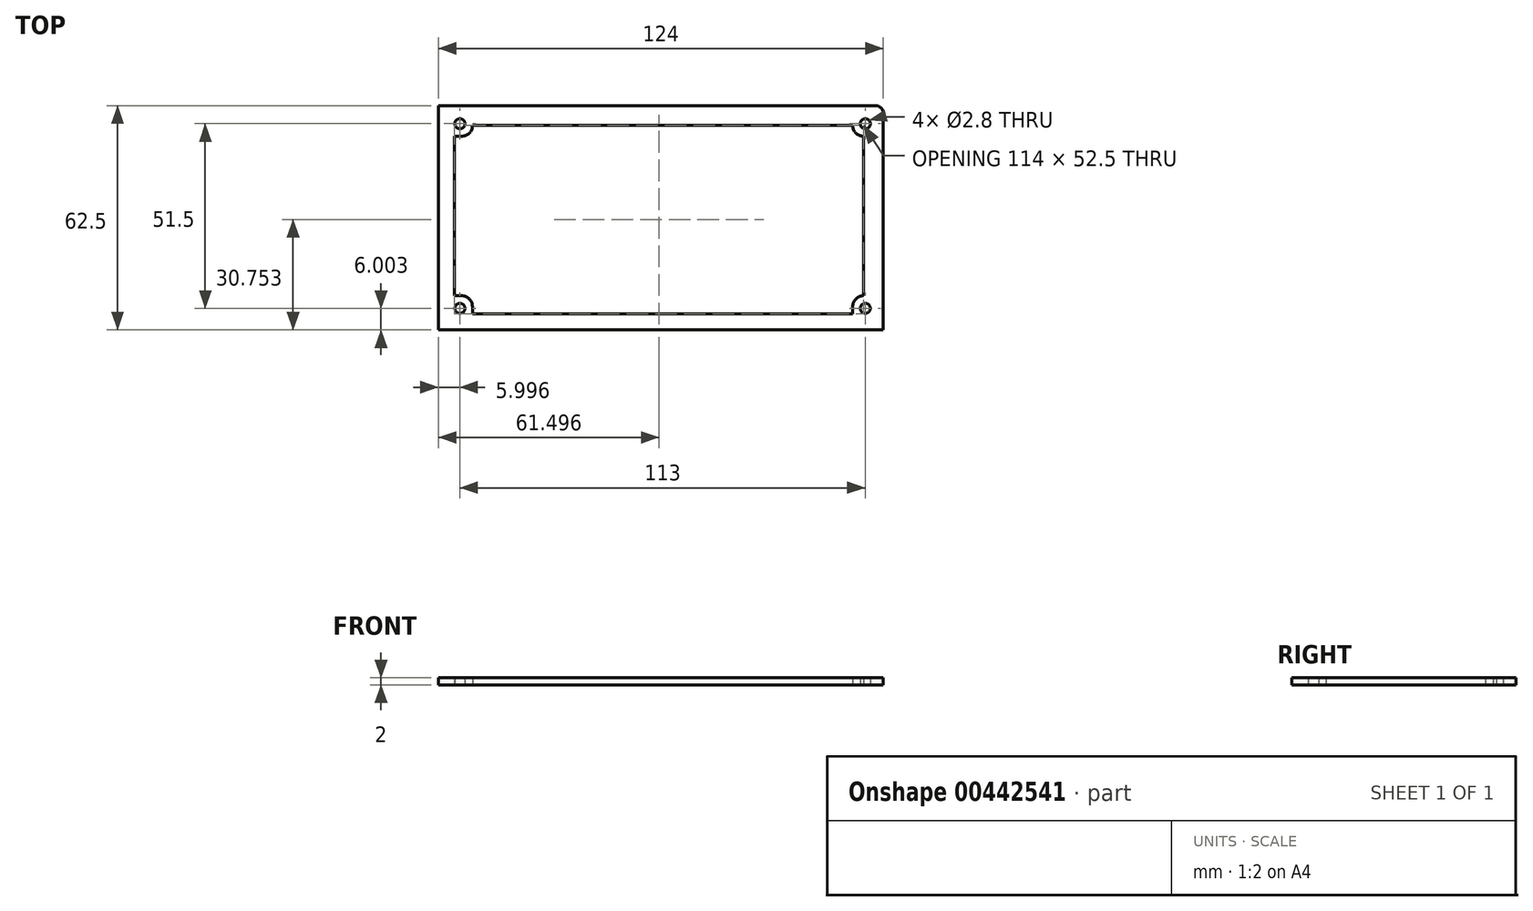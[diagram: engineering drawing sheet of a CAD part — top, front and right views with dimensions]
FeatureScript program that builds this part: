
annotation { "Feature Type Name" : "Feature", "Feature Type Description" : "" }
export const myFeature = defineFeature(function(context is Context, id is Id, definition is map)
    precondition{}
    {
        {
            var Q0;
            Q0=qCreatedBy(makeId("Top.planeOp"),FACE);
            var sketch = newSketch(context, id + "F0", { "sketchPlane" : qUnion([Q0])});
            skLineSegment(sketch, "E0.bottom", {"start": v(-72.45, 22.86) * mm, "end": v(71.55, 22.86) * mm});
            skLineSegment(sketch, "E0.top", {"start": v(-72.45, -61.14) * mm, "end": v(71.55, -61.14) * mm});
            skLineSegment(sketch, "E0.left", {"start": v(-74.45, 20.86) * mm, "end": v(-74.45, -59.14) * mm});
            skLineSegment(sketch, "E0.right", {"start": v(73.55, 20.86) * mm, "end": v(73.55, -59.14) * mm});
            skPoint(sketch, "E1.visualSharp", {"position": v(-74.45, 22.86) * mm});
            skArc(sketch, "E1.filletArc", {"start": v(-72.45, 22.86) * mm, "mid": v(-73.87, 22.28) * mm, "end": v(-74.45, 20.86) * mm});
            skPoint(sketch, "E2.visualSharp", {"position": v(73.55, 22.86) * mm});
            skArc(sketch, "E2.filletArc", {"start": v(73.55, 20.86) * mm, "mid": v(72.96, 22.28) * mm, "end": v(71.55, 22.86) * mm});
            skPoint(sketch, "E3.visualSharp", {"position": v(73.55, -61.14) * mm});
            skArc(sketch, "E3.filletArc", {"start": v(71.55, -61.14) * mm, "mid": v(72.96, -60.55) * mm, "end": v(73.55, -59.14) * mm});
            skPoint(sketch, "E4.visualSharp", {"position": v(-74.45, -61.14) * mm});
            skArc(sketch, "E4.filletArc", {"start": v(-74.45, -59.14) * mm, "mid": v(-73.87, -60.55) * mm, "end": v(-72.45, -61.14) * mm});
            skCircle(sketch, "E5", {"center": v(-69.45, 17.86) * mm, "radius": 1.4 * mm});
            skCircle(sketch, "E6", {"center": v(68.55, 17.86) * mm, "radius": 1.4 * mm});
            skCircle(sketch, "E7", {"center": v(-44.45, 17.86) * mm, "radius": 1.4 * mm});
            skCircle(sketch, "E8", {"center": v(-44.45, -33.64) * mm, "radius": 1.4 * mm});
            skCircle(sketch, "E9", {"center": v(68.55, -33.64) * mm, "radius": 1.4 * mm});
            skCircle(sketch, "E10", {"center": v(-69.45, -56.14) * mm, "radius": 1.4 * mm});
            skCircle(sketch, "E11", {"center": v(44.55, -56.14) * mm, "radius": 1.4 * mm});
            skLineSegment(sketch, "E12.top", {"start": v(-45.95, 14.36) * mm, "end": v(-43.95, 14.36) * mm});
            skLineSegment(sketch, "E13.top", {"start": v(-45.95, -30.14) * mm, "end": v(-43.95, -30.14) * mm});
            skLineSegment(sketch, "E13.right", {"start": v(-40.95, -35.14) * mm, "end": v(-40.95, -33.14) * mm});
            skLineSegment(sketch, "E14.right", {"start": v(65.05, -35.14) * mm, "end": v(65.05, -33.14) * mm});
            skLineSegment(sketch, "E15", {"start": v(65.05, -35.14) * mm, "end": v(-40.95, -35.14) * mm});
            skLineSegment(sketch, "E16", {"start": v(-45.95, -30.14) * mm, "end": v(-45.95, 14.36) * mm});
            skPoint(sketch, "E17.visualSharp", {"position": v(-40.95, 14.36) * mm});
            skArc(sketch, "E17.filletArc", {"start": v(-43.95, 14.36) * mm, "mid": v(-41.83, 15.24) * mm, "end": v(-40.95, 17.36) * mm});
            skPoint(sketch, "E18.visualSharp", {"position": v(65.05, 14.36) * mm});
            skArc(sketch, "E18.filletArc", {"start": v(65.05, 17.36) * mm, "mid": v(65.92, 15.24) * mm, "end": v(68.05, 14.36) * mm});
            skPoint(sketch, "E19.visualSharp", {"position": v(65.05, -30.14) * mm});
            skArc(sketch, "E19.filletArc", {"start": v(68.05, -30.14) * mm, "mid": v(65.92, -31.02) * mm, "end": v(65.05, -33.14) * mm});
            skPoint(sketch, "E20.visualSharp", {"position": v(-40.95, -30.14) * mm});
            skArc(sketch, "E20.filletArc", {"start": v(-40.95, -33.14) * mm, "mid": v(-41.83, -31.02) * mm, "end": v(-43.95, -30.14) * mm});
            skLineSegment(sketch, "E21", {"start": v(68.05, 14.36) * mm, "end": v(68.05, -30.14) * mm});
            skLineSegment(sketch, "E22", {"start": v(65.05, 17.36) * mm, "end": v(-40.95, 17.36) * mm});
            skLineSegment(sketch, "E23.bottom", {"start": v(-66.45, -39.64) * mm, "end": v(-61.95, -39.64) * mm});
            skLineSegment(sketch, "E23.top", {"start": v(-66.45, -44.14) * mm, "end": v(-61.95, -44.14) * mm});
            skLineSegment(sketch, "E23.left", {"start": v(-66.45, -39.64) * mm, "end": v(-66.45, -44.14) * mm});
            skLineSegment(sketch, "E23.right", {"start": v(-61.95, -39.64) * mm, "end": v(-61.95, -44.14) * mm});
            skLineSegment(sketch, "E24.bottom", {"start": v(-66.39, -47.2) * mm, "end": v(-61.89, -47.2) * mm});
            skLineSegment(sketch, "E24.top", {"start": v(-66.39, -51.7) * mm, "end": v(-61.89, -51.7) * mm});
            skLineSegment(sketch, "E24.left", {"start": v(-66.39, -47.2) * mm, "end": v(-66.39, -51.7) * mm});
            skLineSegment(sketch, "E24.right", {"start": v(-61.89, -47.2) * mm, "end": v(-61.89, -51.7) * mm});
            skLineSegment(sketch, "E25.1.0.0", {"start": v(-53.89, -47.2) * mm, "end": v(-53.89, -51.7) * mm});
            skLineSegment(sketch, "E25.1.0.1", {"start": v(-58.39, -47.2) * mm, "end": v(-58.39, -51.7) * mm});
            skLineSegment(sketch, "E25.1.0.2", {"start": v(-58.39, -51.7) * mm, "end": v(-53.89, -51.7) * mm});
            skLineSegment(sketch, "E25.1.0.3", {"start": v(-58.39, -47.2) * mm, "end": v(-53.89, -47.2) * mm});
            skLineSegment(sketch, "E25.1.0.4", {"start": v(-53.95, -39.64) * mm, "end": v(-53.95, -44.14) * mm});
            skLineSegment(sketch, "E25.1.0.5", {"start": v(-58.45, -44.14) * mm, "end": v(-53.95, -44.14) * mm});
            skLineSegment(sketch, "E25.1.0.6", {"start": v(-58.45, -39.64) * mm, "end": v(-58.45, -44.14) * mm});
            skLineSegment(sketch, "E25.1.0.7", {"start": v(-58.45, -39.64) * mm, "end": v(-53.95, -39.64) * mm});
            skLineSegment(sketch, "E25.2.0.0", {"start": v(-45.89, -47.2) * mm, "end": v(-45.89, -51.7) * mm});
            skLineSegment(sketch, "E25.2.0.1", {"start": v(-50.39, -47.2) * mm, "end": v(-50.39, -51.7) * mm});
            skLineSegment(sketch, "E25.2.0.2", {"start": v(-50.39, -51.7) * mm, "end": v(-45.89, -51.7) * mm});
            skLineSegment(sketch, "E25.2.0.3", {"start": v(-50.39, -47.2) * mm, "end": v(-45.89, -47.2) * mm});
            skLineSegment(sketch, "E25.2.0.4", {"start": v(-45.95, -39.64) * mm, "end": v(-45.95, -44.14) * mm});
            skLineSegment(sketch, "E25.2.0.5", {"start": v(-50.45, -44.14) * mm, "end": v(-45.95, -44.14) * mm});
            skLineSegment(sketch, "E25.2.0.6", {"start": v(-50.45, -39.64) * mm, "end": v(-50.45, -44.14) * mm});
            skLineSegment(sketch, "E25.2.0.7", {"start": v(-50.45, -39.64) * mm, "end": v(-45.95, -39.64) * mm});
            skLineSegment(sketch, "E25.3.0.0", {"start": v(-37.89, -47.2) * mm, "end": v(-37.89, -51.7) * mm});
            skLineSegment(sketch, "E25.3.0.1", {"start": v(-42.39, -47.2) * mm, "end": v(-42.39, -51.7) * mm});
            skLineSegment(sketch, "E25.3.0.2", {"start": v(-42.39, -51.7) * mm, "end": v(-37.89, -51.7) * mm});
            skLineSegment(sketch, "E25.3.0.3", {"start": v(-42.39, -47.2) * mm, "end": v(-37.89, -47.2) * mm});
            skLineSegment(sketch, "E25.3.0.4", {"start": v(-37.95, -39.64) * mm, "end": v(-37.95, -44.14) * mm});
            skLineSegment(sketch, "E25.3.0.5", {"start": v(-42.45, -44.14) * mm, "end": v(-37.95, -44.14) * mm});
            skLineSegment(sketch, "E25.3.0.6", {"start": v(-42.45, -39.64) * mm, "end": v(-42.45, -44.14) * mm});
            skLineSegment(sketch, "E25.3.0.7", {"start": v(-42.45, -39.64) * mm, "end": v(-37.95, -39.64) * mm});
            skLineSegment(sketch, "E25.4.0.0", {"start": v(-29.89, -47.2) * mm, "end": v(-29.89, -51.7) * mm});
            skLineSegment(sketch, "E25.4.0.1", {"start": v(-34.39, -47.2) * mm, "end": v(-34.39, -51.7) * mm});
            skLineSegment(sketch, "E25.4.0.2", {"start": v(-34.39, -51.7) * mm, "end": v(-29.89, -51.7) * mm});
            skLineSegment(sketch, "E25.4.0.3", {"start": v(-34.39, -47.2) * mm, "end": v(-29.89, -47.2) * mm});
            skLineSegment(sketch, "E25.4.0.4", {"start": v(-29.95, -39.64) * mm, "end": v(-29.95, -44.14) * mm});
            skLineSegment(sketch, "E25.4.0.5", {"start": v(-34.45, -44.14) * mm, "end": v(-29.95, -44.14) * mm});
            skLineSegment(sketch, "E25.4.0.6", {"start": v(-34.45, -39.64) * mm, "end": v(-34.45, -44.14) * mm});
            skLineSegment(sketch, "E25.4.0.7", {"start": v(-34.45, -39.64) * mm, "end": v(-29.95, -39.64) * mm});
            skLineSegment(sketch, "E25.5.0.0", {"start": v(-21.89, -47.2) * mm, "end": v(-21.89, -51.7) * mm});
            skLineSegment(sketch, "E25.5.0.1", {"start": v(-26.39, -47.2) * mm, "end": v(-26.39, -51.7) * mm});
            skLineSegment(sketch, "E25.5.0.2", {"start": v(-26.39, -51.7) * mm, "end": v(-21.89, -51.7) * mm});
            skLineSegment(sketch, "E25.5.0.3", {"start": v(-26.39, -47.2) * mm, "end": v(-21.89, -47.2) * mm});
            skLineSegment(sketch, "E25.5.0.4", {"start": v(-21.95, -39.64) * mm, "end": v(-21.95, -44.14) * mm});
            skLineSegment(sketch, "E25.5.0.5", {"start": v(-26.45, -44.14) * mm, "end": v(-21.95, -44.14) * mm});
            skLineSegment(sketch, "E25.5.0.6", {"start": v(-26.45, -39.64) * mm, "end": v(-26.45, -44.14) * mm});
            skLineSegment(sketch, "E25.5.0.7", {"start": v(-26.45, -39.64) * mm, "end": v(-21.95, -39.64) * mm});
            skLineSegment(sketch, "E25.6.0.0", {"start": v(-13.89, -47.2) * mm, "end": v(-13.89, -51.7) * mm});
            skLineSegment(sketch, "E25.6.0.1", {"start": v(-18.39, -47.2) * mm, "end": v(-18.39, -51.7) * mm});
            skLineSegment(sketch, "E25.6.0.2", {"start": v(-18.39, -51.7) * mm, "end": v(-13.89, -51.7) * mm});
            skLineSegment(sketch, "E25.6.0.3", {"start": v(-18.39, -47.2) * mm, "end": v(-13.89, -47.2) * mm});
            skLineSegment(sketch, "E25.6.0.4", {"start": v(-13.95, -39.64) * mm, "end": v(-13.95, -44.14) * mm});
            skLineSegment(sketch, "E25.6.0.5", {"start": v(-18.45, -44.14) * mm, "end": v(-13.95, -44.14) * mm});
            skLineSegment(sketch, "E25.6.0.6", {"start": v(-18.45, -39.64) * mm, "end": v(-18.45, -44.14) * mm});
            skLineSegment(sketch, "E25.6.0.7", {"start": v(-18.45, -39.64) * mm, "end": v(-13.95, -39.64) * mm});
            skLineSegment(sketch, "E25.7.0.0", {"start": v(-5.89, -47.2) * mm, "end": v(-5.89, -51.7) * mm});
            skLineSegment(sketch, "E25.7.0.1", {"start": v(-10.39, -47.2) * mm, "end": v(-10.39, -51.7) * mm});
            skLineSegment(sketch, "E25.7.0.2", {"start": v(-10.39, -51.7) * mm, "end": v(-5.89, -51.7) * mm});
            skLineSegment(sketch, "E25.7.0.3", {"start": v(-10.39, -47.2) * mm, "end": v(-5.89, -47.2) * mm});
            skLineSegment(sketch, "E25.7.0.4", {"start": v(-5.95, -39.64) * mm, "end": v(-5.95, -44.14) * mm});
            skLineSegment(sketch, "E25.7.0.5", {"start": v(-10.45, -44.14) * mm, "end": v(-5.95, -44.14) * mm});
            skLineSegment(sketch, "E25.7.0.6", {"start": v(-10.45, -39.64) * mm, "end": v(-10.45, -44.14) * mm});
            skLineSegment(sketch, "E25.7.0.7", {"start": v(-10.45, -39.64) * mm, "end": v(-5.95, -39.64) * mm});
            skLineSegment(sketch, "E25.8.0.0", {"start": v(2.11, -47.2) * mm, "end": v(2.11, -51.7) * mm});
            skLineSegment(sketch, "E25.8.0.1", {"start": v(-2.39, -47.2) * mm, "end": v(-2.39, -51.7) * mm});
            skLineSegment(sketch, "E25.8.0.2", {"start": v(-2.39, -51.7) * mm, "end": v(2.11, -51.7) * mm});
            skLineSegment(sketch, "E25.8.0.3", {"start": v(-2.39, -47.2) * mm, "end": v(2.11, -47.2) * mm});
            skLineSegment(sketch, "E25.8.0.4", {"start": v(2.05, -39.64) * mm, "end": v(2.05, -44.14) * mm});
            skLineSegment(sketch, "E25.8.0.5", {"start": v(-2.45, -44.14) * mm, "end": v(2.05, -44.14) * mm});
            skLineSegment(sketch, "E25.8.0.6", {"start": v(-2.45, -39.64) * mm, "end": v(-2.45, -44.14) * mm});
            skLineSegment(sketch, "E25.8.0.7", {"start": v(-2.45, -39.64) * mm, "end": v(2.05, -39.64) * mm});
            skLineSegment(sketch, "E25.9.0.0", {"start": v(10.11, -47.2) * mm, "end": v(10.11, -51.7) * mm});
            skLineSegment(sketch, "E25.9.0.1", {"start": v(5.61, -47.2) * mm, "end": v(5.61, -51.7) * mm});
            skLineSegment(sketch, "E25.9.0.2", {"start": v(5.61, -51.7) * mm, "end": v(10.11, -51.7) * mm});
            skLineSegment(sketch, "E25.9.0.3", {"start": v(5.61, -47.2) * mm, "end": v(10.11, -47.2) * mm});
            skLineSegment(sketch, "E25.9.0.4", {"start": v(10.05, -39.64) * mm, "end": v(10.05, -44.14) * mm});
            skLineSegment(sketch, "E25.9.0.5", {"start": v(5.55, -44.14) * mm, "end": v(10.05, -44.14) * mm});
            skLineSegment(sketch, "E25.9.0.6", {"start": v(5.55, -39.64) * mm, "end": v(5.55, -44.14) * mm});
            skLineSegment(sketch, "E25.9.0.7", {"start": v(5.55, -39.64) * mm, "end": v(10.05, -39.64) * mm});
            skLineSegment(sketch, "E25.10.0.0", {"start": v(18.11, -47.2) * mm, "end": v(18.11, -51.7) * mm});
            skLineSegment(sketch, "E25.10.0.1", {"start": v(13.61, -47.2) * mm, "end": v(13.61, -51.7) * mm});
            skLineSegment(sketch, "E25.10.0.2", {"start": v(13.61, -51.7) * mm, "end": v(18.11, -51.7) * mm});
            skLineSegment(sketch, "E25.10.0.3", {"start": v(13.61, -47.2) * mm, "end": v(18.11, -47.2) * mm});
            skLineSegment(sketch, "E25.10.0.4", {"start": v(18.05, -39.64) * mm, "end": v(18.05, -44.14) * mm});
            skLineSegment(sketch, "E25.10.0.5", {"start": v(13.55, -44.14) * mm, "end": v(18.05, -44.14) * mm});
            skLineSegment(sketch, "E25.10.0.6", {"start": v(13.55, -39.64) * mm, "end": v(13.55, -44.14) * mm});
            skLineSegment(sketch, "E25.10.0.7", {"start": v(13.55, -39.64) * mm, "end": v(18.05, -39.64) * mm});
            skLineSegment(sketch, "E25.11.0.0", {"start": v(26.11, -47.2) * mm, "end": v(26.11, -51.7) * mm});
            skLineSegment(sketch, "E25.11.0.1", {"start": v(21.61, -47.2) * mm, "end": v(21.61, -51.7) * mm});
            skLineSegment(sketch, "E25.11.0.2", {"start": v(21.61, -51.7) * mm, "end": v(26.11, -51.7) * mm});
            skLineSegment(sketch, "E25.11.0.3", {"start": v(21.61, -47.2) * mm, "end": v(26.11, -47.2) * mm});
            skLineSegment(sketch, "E25.11.0.4", {"start": v(26.05, -39.64) * mm, "end": v(26.05, -44.14) * mm});
            skLineSegment(sketch, "E25.11.0.5", {"start": v(21.55, -44.14) * mm, "end": v(26.05, -44.14) * mm});
            skLineSegment(sketch, "E25.11.0.6", {"start": v(21.55, -39.64) * mm, "end": v(21.55, -44.14) * mm});
            skLineSegment(sketch, "E25.11.0.7", {"start": v(21.55, -39.64) * mm, "end": v(26.05, -39.64) * mm});
            skLineSegment(sketch, "E25.12.0.0", {"start": v(34.11, -47.2) * mm, "end": v(34.11, -51.7) * mm});
            skLineSegment(sketch, "E25.12.0.1", {"start": v(29.61, -47.2) * mm, "end": v(29.61, -51.7) * mm});
            skLineSegment(sketch, "E25.12.0.2", {"start": v(29.61, -51.7) * mm, "end": v(34.11, -51.7) * mm});
            skLineSegment(sketch, "E25.12.0.3", {"start": v(29.61, -47.2) * mm, "end": v(34.11, -47.2) * mm});
            skLineSegment(sketch, "E25.12.0.4", {"start": v(34.05, -39.64) * mm, "end": v(34.05, -44.14) * mm});
            skLineSegment(sketch, "E25.12.0.5", {"start": v(29.55, -44.14) * mm, "end": v(34.05, -44.14) * mm});
            skLineSegment(sketch, "E25.12.0.6", {"start": v(29.55, -39.64) * mm, "end": v(29.55, -44.14) * mm});
            skLineSegment(sketch, "E25.12.0.7", {"start": v(29.55, -39.64) * mm, "end": v(34.05, -39.64) * mm});
            skLineSegment(sketch, "E25.13.0.0", {"start": v(42.11, -47.2) * mm, "end": v(42.11, -51.7) * mm});
            skLineSegment(sketch, "E25.13.0.1", {"start": v(37.61, -47.2) * mm, "end": v(37.61, -51.7) * mm});
            skLineSegment(sketch, "E25.13.0.2", {"start": v(37.61, -51.7) * mm, "end": v(42.11, -51.7) * mm});
            skLineSegment(sketch, "E25.13.0.3", {"start": v(37.61, -47.2) * mm, "end": v(42.11, -47.2) * mm});
            skLineSegment(sketch, "E25.13.0.4", {"start": v(42.05, -39.64) * mm, "end": v(42.05, -44.14) * mm});
            skLineSegment(sketch, "E25.13.0.5", {"start": v(37.55, -44.14) * mm, "end": v(42.05, -44.14) * mm});
            skLineSegment(sketch, "E25.13.0.6", {"start": v(37.55, -39.64) * mm, "end": v(37.55, -44.14) * mm});
            skLineSegment(sketch, "E25.13.0.7", {"start": v(37.55, -39.64) * mm, "end": v(42.05, -39.64) * mm});
            skLineSegment(sketch, "E25.14.0.0", {"start": v(50.11, -47.2) * mm, "end": v(50.11, -51.7) * mm});
            skLineSegment(sketch, "E25.14.0.1", {"start": v(45.61, -47.2) * mm, "end": v(45.61, -51.7) * mm});
            skLineSegment(sketch, "E25.14.0.2", {"start": v(45.61, -51.7) * mm, "end": v(50.11, -51.7) * mm});
            skLineSegment(sketch, "E25.14.0.3", {"start": v(45.61, -47.2) * mm, "end": v(50.11, -47.2) * mm});
            skLineSegment(sketch, "E25.14.0.4", {"start": v(50.05, -39.64) * mm, "end": v(50.05, -44.14) * mm});
            skLineSegment(sketch, "E25.14.0.5", {"start": v(45.55, -44.14) * mm, "end": v(50.05, -44.14) * mm});
            skLineSegment(sketch, "E25.14.0.6", {"start": v(45.55, -39.64) * mm, "end": v(45.55, -44.14) * mm});
            skLineSegment(sketch, "E25.14.0.7", {"start": v(45.55, -39.64) * mm, "end": v(50.05, -39.64) * mm});
            skLineSegment(sketch, "E25.15.0.0", {"start": v(58.11, -47.2) * mm, "end": v(58.11, -51.7) * mm});
            skLineSegment(sketch, "E25.15.0.1", {"start": v(53.61, -47.2) * mm, "end": v(53.61, -51.7) * mm});
            skLineSegment(sketch, "E25.15.0.2", {"start": v(53.61, -51.7) * mm, "end": v(58.11, -51.7) * mm});
            skLineSegment(sketch, "E25.15.0.3", {"start": v(53.61, -47.2) * mm, "end": v(58.11, -47.2) * mm});
            skLineSegment(sketch, "E25.15.0.4", {"start": v(58.05, -39.64) * mm, "end": v(58.05, -44.14) * mm});
            skLineSegment(sketch, "E25.15.0.5", {"start": v(53.55, -44.14) * mm, "end": v(58.05, -44.14) * mm});
            skLineSegment(sketch, "E25.15.0.6", {"start": v(53.55, -39.64) * mm, "end": v(53.55, -44.14) * mm});
            skLineSegment(sketch, "E25.15.0.7", {"start": v(53.55, -39.64) * mm, "end": v(58.05, -39.64) * mm});
            skLineSegment(sketch, "E25.16.0.0", {"start": v(66.11, -47.2) * mm, "end": v(66.11, -51.7) * mm});
            skLineSegment(sketch, "E25.16.0.1", {"start": v(61.61, -47.2) * mm, "end": v(61.61, -51.7) * mm});
            skLineSegment(sketch, "E25.16.0.2", {"start": v(61.61, -51.7) * mm, "end": v(66.11, -51.7) * mm});
            skLineSegment(sketch, "E25.16.0.3", {"start": v(61.61, -47.2) * mm, "end": v(66.11, -47.2) * mm});
            skLineSegment(sketch, "E25.16.0.4", {"start": v(66.05, -39.64) * mm, "end": v(66.05, -44.14) * mm});
            skLineSegment(sketch, "E25.16.0.5", {"start": v(61.55, -44.14) * mm, "end": v(66.05, -44.14) * mm});
            skLineSegment(sketch, "E25.16.0.6", {"start": v(61.55, -39.64) * mm, "end": v(61.55, -44.14) * mm});
            skLineSegment(sketch, "E25.16.0.7", {"start": v(61.55, -39.64) * mm, "end": v(66.05, -39.64) * mm});
            skLineSegment(sketch, "E25.direction1", {"start": v(-66.39, -51.7) * mm, "end": v(-58.39, -51.7) * mm, "construction": true});
            skSolve(sketch);
        }
        {
            var Q0;
            Q0=makeQuery(id+"F0.imprint","IMPRINT",FACE,{"disambiguationData":[TD([[makeQuery(id+"F0.imprint","IMPRINT",EDGE,{"derivedFrom":sQuery(id+"F0.wireOp",EDGE,"E0.bottom")}),-1.0]])]});
            extrude(context, id + "F1", {"entities" : qUnion([Q0]), "depth" : 2 * mm});
        }
        {
            var Q0;
            Q0=makeQuery(id+"F1.opExtrude","CAP_FACE",FACE,{"disambiguationData":[OSD([sQuery(id+"F0.wireOp",EDGE,"E0.bottom"),sQuery(id+"F0.wireOp",EDGE,"E0.top"),sQuery(id+"F0.wireOp",EDGE,"E0.left"),sQuery(id+"F0.wireOp",EDGE,"E0.right"),sQuery(id+"F0.wireOp",EDGE,"E1.filletArc"),sQuery(id+"F0.wireOp",EDGE,"E2.filletArc"),sQuery(id+"F0.wireOp",EDGE,"E3.filletArc"),sQuery(id+"F0.wireOp",EDGE,"E4.filletArc"),sQuery(id+"F0.wireOp",EDGE,"E5"),sQuery(id+"F0.wireOp",EDGE,"E6"),sQuery(id+"F0.wireOp",EDGE,"E7"),sQuery(id+"F0.wireOp",EDGE,"E8"),sQuery(id+"F0.wireOp",EDGE,"E9"),sQuery(id+"F0.wireOp",EDGE,"E10"),sQuery(id+"F0.wireOp",EDGE,"E11"),sQuery(id+"F0.wireOp",EDGE,"E12.top"),sQuery(id+"F0.wireOp",EDGE,"E13.top"),sQuery(id+"F0.wireOp",EDGE,"E13.right"),sQuery(id+"F0.wireOp",EDGE,"E14.right"),sQuery(id+"F0.wireOp",EDGE,"E15"),sQuery(id+"F0.wireOp",EDGE,"E16"),sQuery(id+"F0.wireOp",EDGE,"E17.filletArc"),sQuery(id+"F0.wireOp",EDGE,"E18.filletArc"),sQuery(id+"F0.wireOp",EDGE,"E19.filletArc"),sQuery(id+"F0.wireOp",EDGE,"E20.filletArc"),sQuery(id+"F0.wireOp",EDGE,"E21"),sQuery(id+"F0.wireOp",EDGE,"E22"),sQuery(id+"F0.wireOp",EDGE,"E23.bottom"),sQuery(id+"F0.wireOp",EDGE,"E23.top"),sQuery(id+"F0.wireOp",EDGE,"E23.left"),sQuery(id+"F0.wireOp",EDGE,"E23.right"),sQuery(id+"F0.wireOp",EDGE,"E24.bottom"),sQuery(id+"F0.wireOp",EDGE,"E24.top"),sQuery(id+"F0.wireOp",EDGE,"E24.left"),sQuery(id+"F0.wireOp",EDGE,"E24.right"),sQuery(id+"F0.wireOp",EDGE,"E25.1.0.0"),sQuery(id+"F0.wireOp",EDGE,"E25.1.0.1"),sQuery(id+"F0.wireOp",EDGE,"E25.1.0.2"),sQuery(id+"F0.wireOp",EDGE,"E25.1.0.3"),sQuery(id+"F0.wireOp",EDGE,"E25.1.0.4"),sQuery(id+"F0.wireOp",EDGE,"E25.1.0.5"),sQuery(id+"F0.wireOp",EDGE,"E25.1.0.6"),sQuery(id+"F0.wireOp",EDGE,"E25.1.0.7"),sQuery(id+"F0.wireOp",EDGE,"E25.2.0.0"),sQuery(id+"F0.wireOp",EDGE,"E25.2.0.1"),sQuery(id+"F0.wireOp",EDGE,"E25.2.0.2"),sQuery(id+"F0.wireOp",EDGE,"E25.2.0.3"),sQuery(id+"F0.wireOp",EDGE,"E25.2.0.4"),sQuery(id+"F0.wireOp",EDGE,"E25.2.0.5"),sQuery(id+"F0.wireOp",EDGE,"E25.2.0.6"),sQuery(id+"F0.wireOp",EDGE,"E25.2.0.7"),sQuery(id+"F0.wireOp",EDGE,"E25.3.0.0"),sQuery(id+"F0.wireOp",EDGE,"E25.3.0.1"),sQuery(id+"F0.wireOp",EDGE,"E25.3.0.2"),sQuery(id+"F0.wireOp",EDGE,"E25.3.0.3"),sQuery(id+"F0.wireOp",EDGE,"E25.3.0.4"),sQuery(id+"F0.wireOp",EDGE,"E25.3.0.5"),sQuery(id+"F0.wireOp",EDGE,"E25.3.0.6"),sQuery(id+"F0.wireOp",EDGE,"E25.3.0.7"),sQuery(id+"F0.wireOp",EDGE,"E25.4.0.0"),sQuery(id+"F0.wireOp",EDGE,"E25.4.0.1"),sQuery(id+"F0.wireOp",EDGE,"E25.4.0.2"),sQuery(id+"F0.wireOp",EDGE,"E25.4.0.3"),sQuery(id+"F0.wireOp",EDGE,"E25.4.0.4"),sQuery(id+"F0.wireOp",EDGE,"E25.4.0.5"),sQuery(id+"F0.wireOp",EDGE,"E25.4.0.6"),sQuery(id+"F0.wireOp",EDGE,"E25.4.0.7"),sQuery(id+"F0.wireOp",EDGE,"E25.5.0.0"),sQuery(id+"F0.wireOp",EDGE,"E25.5.0.1"),sQuery(id+"F0.wireOp",EDGE,"E25.5.0.2"),sQuery(id+"F0.wireOp",EDGE,"E25.5.0.3"),sQuery(id+"F0.wireOp",EDGE,"E25.5.0.4"),sQuery(id+"F0.wireOp",EDGE,"E25.5.0.5"),sQuery(id+"F0.wireOp",EDGE,"E25.5.0.6"),sQuery(id+"F0.wireOp",EDGE,"E25.5.0.7"),sQuery(id+"F0.wireOp",EDGE,"E25.6.0.0"),sQuery(id+"F0.wireOp",EDGE,"E25.6.0.1"),sQuery(id+"F0.wireOp",EDGE,"E25.6.0.2"),sQuery(id+"F0.wireOp",EDGE,"E25.6.0.3"),sQuery(id+"F0.wireOp",EDGE,"E25.6.0.4"),sQuery(id+"F0.wireOp",EDGE,"E25.6.0.5"),sQuery(id+"F0.wireOp",EDGE,"E25.6.0.6"),sQuery(id+"F0.wireOp",EDGE,"E25.6.0.7"),sQuery(id+"F0.wireOp",EDGE,"E25.7.0.0"),sQuery(id+"F0.wireOp",EDGE,"E25.7.0.1"),sQuery(id+"F0.wireOp",EDGE,"E25.7.0.2"),sQuery(id+"F0.wireOp",EDGE,"E25.7.0.3"),sQuery(id+"F0.wireOp",EDGE,"E25.7.0.4"),sQuery(id+"F0.wireOp",EDGE,"E25.7.0.5"),sQuery(id+"F0.wireOp",EDGE,"E25.7.0.6"),sQuery(id+"F0.wireOp",EDGE,"E25.7.0.7"),sQuery(id+"F0.wireOp",EDGE,"E25.8.0.0"),sQuery(id+"F0.wireOp",EDGE,"E25.8.0.1"),sQuery(id+"F0.wireOp",EDGE,"E25.8.0.2"),sQuery(id+"F0.wireOp",EDGE,"E25.8.0.3"),sQuery(id+"F0.wireOp",EDGE,"E25.8.0.4"),sQuery(id+"F0.wireOp",EDGE,"E25.8.0.5"),sQuery(id+"F0.wireOp",EDGE,"E25.8.0.6"),sQuery(id+"F0.wireOp",EDGE,"E25.8.0.7"),sQuery(id+"F0.wireOp",EDGE,"E25.9.0.0"),sQuery(id+"F0.wireOp",EDGE,"E25.9.0.1"),sQuery(id+"F0.wireOp",EDGE,"E25.9.0.2"),sQuery(id+"F0.wireOp",EDGE,"E25.9.0.3"),sQuery(id+"F0.wireOp",EDGE,"E25.9.0.4"),sQuery(id+"F0.wireOp",EDGE,"E25.9.0.5"),sQuery(id+"F0.wireOp",EDGE,"E25.9.0.6"),sQuery(id+"F0.wireOp",EDGE,"E25.9.0.7"),sQuery(id+"F0.wireOp",EDGE,"E25.10.0.0"),sQuery(id+"F0.wireOp",EDGE,"E25.10.0.1"),sQuery(id+"F0.wireOp",EDGE,"E25.10.0.2"),sQuery(id+"F0.wireOp",EDGE,"E25.10.0.3"),sQuery(id+"F0.wireOp",EDGE,"E25.10.0.4"),sQuery(id+"F0.wireOp",EDGE,"E25.10.0.5"),sQuery(id+"F0.wireOp",EDGE,"E25.10.0.6"),sQuery(id+"F0.wireOp",EDGE,"E25.10.0.7"),sQuery(id+"F0.wireOp",EDGE,"E25.11.0.0"),sQuery(id+"F0.wireOp",EDGE,"E25.11.0.1"),sQuery(id+"F0.wireOp",EDGE,"E25.11.0.2"),sQuery(id+"F0.wireOp",EDGE,"E25.11.0.3"),sQuery(id+"F0.wireOp",EDGE,"E25.11.0.4"),sQuery(id+"F0.wireOp",EDGE,"E25.11.0.5"),sQuery(id+"F0.wireOp",EDGE,"E25.11.0.6"),sQuery(id+"F0.wireOp",EDGE,"E25.11.0.7"),sQuery(id+"F0.wireOp",EDGE,"E25.12.0.0"),sQuery(id+"F0.wireOp",EDGE,"E25.12.0.1"),sQuery(id+"F0.wireOp",EDGE,"E25.12.0.2"),sQuery(id+"F0.wireOp",EDGE,"E25.12.0.3"),sQuery(id+"F0.wireOp",EDGE,"E25.12.0.4"),sQuery(id+"F0.wireOp",EDGE,"E25.12.0.5"),sQuery(id+"F0.wireOp",EDGE,"E25.12.0.6"),sQuery(id+"F0.wireOp",EDGE,"E25.12.0.7"),sQuery(id+"F0.wireOp",EDGE,"E25.13.0.0"),sQuery(id+"F0.wireOp",EDGE,"E25.13.0.1"),sQuery(id+"F0.wireOp",EDGE,"E25.13.0.2"),sQuery(id+"F0.wireOp",EDGE,"E25.13.0.3"),sQuery(id+"F0.wireOp",EDGE,"E25.13.0.4"),sQuery(id+"F0.wireOp",EDGE,"E25.13.0.5"),sQuery(id+"F0.wireOp",EDGE,"E25.13.0.6"),sQuery(id+"F0.wireOp",EDGE,"E25.13.0.7"),sQuery(id+"F0.wireOp",EDGE,"E25.14.0.0"),sQuery(id+"F0.wireOp",EDGE,"E25.14.0.1"),sQuery(id+"F0.wireOp",EDGE,"E25.14.0.2"),sQuery(id+"F0.wireOp",EDGE,"E25.14.0.3"),sQuery(id+"F0.wireOp",EDGE,"E25.14.0.4"),sQuery(id+"F0.wireOp",EDGE,"E25.14.0.5"),sQuery(id+"F0.wireOp",EDGE,"E25.14.0.6"),sQuery(id+"F0.wireOp",EDGE,"E25.14.0.7"),sQuery(id+"F0.wireOp",EDGE,"E25.15.0.0"),sQuery(id+"F0.wireOp",EDGE,"E25.15.0.1"),sQuery(id+"F0.wireOp",EDGE,"E25.15.0.2"),sQuery(id+"F0.wireOp",EDGE,"E25.15.0.3"),sQuery(id+"F0.wireOp",EDGE,"E25.15.0.4"),sQuery(id+"F0.wireOp",EDGE,"E25.15.0.5"),sQuery(id+"F0.wireOp",EDGE,"E25.15.0.6"),sQuery(id+"F0.wireOp",EDGE,"E25.15.0.7"),sQuery(id+"F0.wireOp",EDGE,"E25.16.0.0"),sQuery(id+"F0.wireOp",EDGE,"E25.16.0.1"),sQuery(id+"F0.wireOp",EDGE,"E25.16.0.2"),sQuery(id+"F0.wireOp",EDGE,"E25.16.0.3"),sQuery(id+"F0.wireOp",EDGE,"E25.16.0.4"),sQuery(id+"F0.wireOp",EDGE,"E25.16.0.5"),sQuery(id+"F0.wireOp",EDGE,"E25.16.0.6"),sQuery(id+"F0.wireOp",EDGE,"E25.16.0.7")])],"isStart":false});
            var sketch = newSketch(context, id + "F2", { "sketchPlane" : qUnion([Q0])});
            skLineSegment(sketch, "E26.bottom", {"start": v(79.09, 29.32) * mm, "end": v(-50.45, 29.32) * mm});
            skLineSegment(sketch, "E26.top", {"start": v(79.09, -39.64) * mm, "end": v(-50.45, -39.64) * mm});
            skLineSegment(sketch, "E26.left", {"start": v(79.09, 29.32) * mm, "end": v(79.09, -39.64) * mm});
            skLineSegment(sketch, "E26.right", {"start": v(-50.45, 29.32) * mm, "end": v(-50.45, -39.64) * mm});
            skSolve(sketch);
        }
        {
            var Q0;
            Q0=makeQuery(id+"F2.imprint","IMPRINT",FACE,{"disambiguationData":[TD([[makeQuery(id+"F2.imprint","IMPRINT",EDGE,{"derivedFrom":makeQuery(id+"F1.opExtrude","CAP_EDGE",EDGE,{"disambiguationData":[OSD([sQuery(id+"F0.wireOp",EDGE,"E0.top")])],"isStart":false})}),1.0]])]});
            extrude(context, id + "F3", {"entities" : qUnion([Q0]), "operationType" : NewBodyOperationType.REMOVE, "oppositeDirection" : true, "depth" : 25 * mm});
        }
    });
